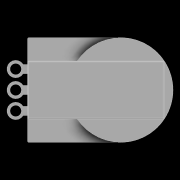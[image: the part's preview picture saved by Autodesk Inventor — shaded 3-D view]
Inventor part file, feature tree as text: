
AUTODESK INVENTOR PART (.ipt)
format: ipt  version: 2020 (Build 240168000, 168)  size: 275,456 bytes
history: native  units: in
note: dims shown in document units (in); Inventor stores cm internally (conversion verified against a paired STEP export)
features: other x10, extrude x9, fillet x2
ambient origin geometry x8: Origin, YZ Plane, XZ Plane, XY Plane, X Axis, Y Axis, Z Axis, Center Point
bodies: Body1 (feature_tree)
feature tree (21):
  other  "Fishman25KPot"
  extrude  "Fishman25KPotFeature"  Depth=0.2591in
  extrude  "Fishman25KPotBodyFeature"  Depth=0.05in
  other  "Fishman25KPotBodyPlane"
  extrude  "Fishman25KPotBoardFeature"  Depth=0.25in TaperAngle=0.0deg
  extrude  "Fishman25KPotTerminalFeature"  Depth=0.5in
  extrude  "Fishman25KPotMountFeature"  Depth=0.5in TaperAngle=0.0deg
  extrude  "Fishman25KPotNutFeature"  [1 undecoded]
  extrude  "Fishman25KPotTerminalHolesFeature"  Depth=0.05in TaperAngle=0.0deg
  extrude  "Fishman25KPotNeckFeature"  Depth=0.05in TaperAngle=0.0deg
  extrude  "Fishman25KPotKnobFeature"  Depth=0.5in
  fillet  "Fishman25KPotKnobFilletFeature"  Radius=0.05in
  fillet  "CornerFilletsFeature"  Radius=0.05in
  other  "Fishman25KPotBody"
  other  "Fishman25KPotBoard"
  other  "Fishman25KPotTerminal"
  other  "Fishman25KPotMount"
  other  "Fishman25KPotNut"
  other  "Fishman25KPotNeck"
  other  "Fishman25KPotTerminalHoles"
  other  "Fishman25KPotKnob"
note: 1 required parameter value undecoded (feature->parameter linkage not recoverable at this tier; creation-order binding heuristic only, values carry confidence <= 0.55)
